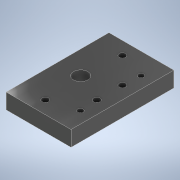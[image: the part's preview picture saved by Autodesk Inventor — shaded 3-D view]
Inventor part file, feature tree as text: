
AUTODESK INVENTOR PART (.ipt)
format: ipt  version: 2022 (Build 260153000, 153)  size: 157,696 bytes
history: native  units: mm
features: sketch x3, extrude x2, projected_geometry x1
ambient origin geometry x8: Origin, YZ Plane, XZ Plane, XY Plane, X Axis, Y Axis, Z Axis, Center Point
bodies: Solid1 (feature_tree)
feature tree (6):
  extrude  "Extrusion1"  Depth=80.0mm
  extrude  "Extrusion2"  Depth=10.0mm
  sketch  "Sketch3"  dims[d4=30.0mm d5=20.0mm d6=5.0mm d7=5.0mm d8=16.4mm d9=16.4mm d10=4.2mm d11=4.2mm d12=32.5mm d13=11.2mm d14=10.0mm d15=30.0mm d16=60.0mm d17=5.0mm d18=12.0mm d19=0.0mm d20=9.9mm d21=19.8mm d22=6.0mm d23=4.2mm d24=4.2mm d25=7.0mm d26=0.0mm d27=47.2mm]
  sketch  "Sketch1"  dims[d0=50.5mm d1=80.0mm]
  sketch  "Sketch2"  dims[d2=9.1mm d3=10.0mm]
  projected_geometry  "Projected Loop1"
